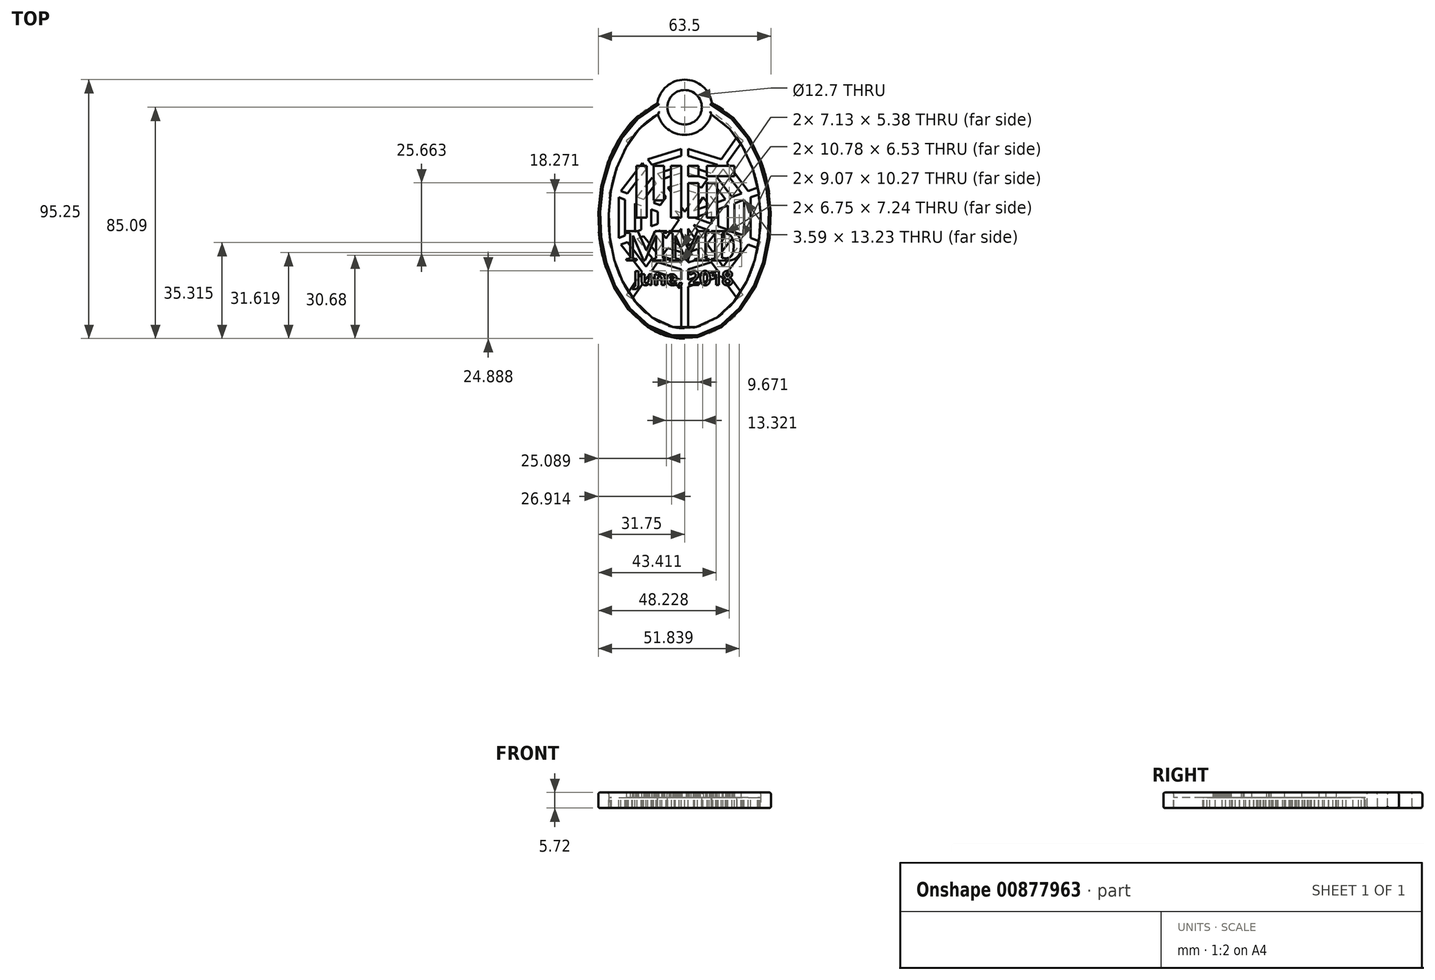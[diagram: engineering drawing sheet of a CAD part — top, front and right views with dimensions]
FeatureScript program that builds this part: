
annotation { "Feature Type Name" : "Feature", "Feature Type Description" : "" }
export const myFeature = defineFeature(function(context is Context, id is Id, definition is map)
    precondition{}
    {
        {
            var Q0;
            Q0=qCreatedBy(makeId("Front.planeOp"),FACE);
            var sketch = newSketch(context, id + "F0", { "sketchPlane" : qUnion([Q0])});
            skLineSegment(sketch, "E0.bottom", {"start": v(31.78, 0) * mm, "end": v(36.86, 0) * mm});
            skLineSegment(sketch, "E0.top", {"start": v(31.78, 5.08) * mm, "end": v(36.86, 5.08) * mm});
            skLineSegment(sketch, "E0.left", {"start": v(31.78, 0) * mm, "end": v(31.78, 5.08) * mm});
            skLineSegment(sketch, "E0.right", {"start": v(36.86, 0) * mm, "end": v(36.86, 5.08) * mm});
            skSolve(sketch);
        }
        {
            var Q0;
            Q0=qCreatedBy(makeId("Top.planeOp"),FACE);
            var sketch = newSketch(context, id + "F1", { "sketchPlane" : qUnion([Q0])});
            skLineSegment(sketch, "E1.bottom", {"start": v(1.27, 40.64) * mm, "end": v(-1.27, 40.64) * mm});
            skLineSegment(sketch, "E1.top", {"start": v(1.27, -40.64) * mm, "end": v(-1.27, -40.64) * mm});
            skLineSegment(sketch, "E1.left", {"start": v(1.27, 40.64) * mm, "end": v(1.27, -40.64) * mm});
            skLineSegment(sketch, "E1.right", {"start": v(-1.27, 40.64) * mm, "end": v(-1.27, -40.64) * mm});
            skPoint(sketch, "E1.middle", {"position": v(0, 0) * mm});
            skLineSegment(sketch, "E2.bottom", {"start": v(21.44, 28.4) * mm, "end": v(19.36, 29.86) * mm});
            skLineSegment(sketch, "E2.top", {"start": v(-19.36, -29.86) * mm, "end": v(-21.44, -28.4) * mm});
            skLineSegment(sketch, "E2.left", {"start": v(21.44, 28.4) * mm, "end": v(-19.36, -29.86) * mm});
            skLineSegment(sketch, "E2.right", {"start": v(19.36, 29.86) * mm, "end": v(-21.44, -28.4) * mm});
            skLineSegment(sketch, "E3.MirrorCS", {"start": v(-19.36, 29.86) * mm, "end": v(-21.44, 28.4) * mm});
            skLineSegment(sketch, "E4.MirrorCS", {"start": v(21.44, -28.4) * mm, "end": v(-19.36, 29.86) * mm});
            skLineSegment(sketch, "E5.MirrorCS", {"start": v(21.44, -28.4) * mm, "end": v(19.36, -29.86) * mm});
            skLineSegment(sketch, "E6.MirrorCS", {"start": v(19.36, -29.86) * mm, "end": v(-21.44, 28.4) * mm});
            skLineSegment(sketch, "E7.bottom", {"start": v(-27.01, -11.18) * mm, "end": v(-27.88, -8.8) * mm});
            skLineSegment(sketch, "E7.top", {"start": v(27.88, 8.8) * mm, "end": v(27.01, 11.18) * mm});
            skLineSegment(sketch, "E7.left", {"start": v(-27.01, -11.18) * mm, "end": v(27.88, 8.8) * mm});
            skLineSegment(sketch, "E7.right", {"start": v(-27.88, -8.8) * mm, "end": v(27.01, 11.18) * mm});
            skEllipse(sketch, "E8", {"center": v(0, 0) * mm, "majorRadius": 44.45 * mm, "minorRadius": 31.75 * mm, "majorAxis": v(0, 1)});
            skLineSegment(sketch, "E9.MirrorCS", {"start": v(-27.01, 11.18) * mm, "end": v(-27.88, 8.8) * mm});
            skLineSegment(sketch, "E10.MirrorCS", {"start": v(-27.88, 8.8) * mm, "end": v(27.01, -11.18) * mm});
            skLineSegment(sketch, "E11.MirrorCS", {"start": v(-27.01, 11.18) * mm, "end": v(27.88, -8.8) * mm});
            skLineSegment(sketch, "E12.MirrorCS", {"start": v(27.88, -8.8) * mm, "end": v(27.01, -11.18) * mm});
            skEllipse(sketch, "E13", {"center": v(0, 0) * mm, "majorRadius": 40.64 * mm, "minorRadius": 27.94 * mm, "majorAxis": v(0, 1)});
            skCircle(sketch, "E14", {"center": v(0, 40.64) * mm, "radius": 6.35 * mm});
            skCircle(sketch, "E15", {"center": v(0, 40.64) * mm, "radius": 10.16 * mm});
            skLineSegment(sketch, "E16", {"start": v(-23.4, 9.87) * mm, "end": v(-15.6, 20.05) * mm});
            skLineSegment(sketch, "E17", {"start": v(-15.6, 20.05) * mm, "end": v(-14.13, 17.97) * mm});
            skLineSegment(sketch, "E18", {"start": v(-14.13, 17.97) * mm, "end": v(-21.01, 9) * mm});
            skLineSegment(sketch, "E19", {"start": v(-21.01, 9) * mm, "end": v(-17.43, 7.7) * mm});
            skLineSegment(sketch, "E20", {"start": v(-17.43, 7.7) * mm, "end": v(-11.94, 14.84) * mm});
            skLineSegment(sketch, "E21", {"start": v(-11.94, 14.84) * mm, "end": v(-10.48, 12.76) * mm});
            skLineSegment(sketch, "E22", {"start": v(-10.48, 12.76) * mm, "end": v(-15.03, 6.82) * mm});
            skLineSegment(sketch, "E23", {"start": v(-15.03, 6.82) * mm, "end": v(-11.44, 5.52) * mm});
            skLineSegment(sketch, "E24", {"start": v(-11.44, 5.52) * mm, "end": v(-8.29, 9.62) * mm});
            skLineSegment(sketch, "E25", {"start": v(-8.29, 9.62) * mm, "end": v(-6.82, 7.53) * mm});
            skLineSegment(sketch, "E26", {"start": v(-6.82, 7.53) * mm, "end": v(-9.04, 4.64) * mm});
            skLineSegment(sketch, "E27", {"start": v(-13.51, 21.5) * mm, "end": v(-1.27, 25.37) * mm});
            skLineSegment(sketch, "E28", {"start": v(-1.27, 25.37) * mm, "end": v(-1.27, 22.82) * mm});
            skLineSegment(sketch, "E29", {"start": v(-1.27, 22.82) * mm, "end": v(-12.05, 19.43) * mm});
            skLineSegment(sketch, "E30", {"start": v(-12.05, 19.43) * mm, "end": v(-9.86, 16.3) * mm});
            skLineSegment(sketch, "E31", {"start": v(-9.86, 16.3) * mm, "end": v(-1.27, 19) * mm});
            skLineSegment(sketch, "E32", {"start": v(-1.27, 19) * mm, "end": v(-1.27, 16.46) * mm});
            skLineSegment(sketch, "E33", {"start": v(-1.27, 16.46) * mm, "end": v(-8.4, 14.21) * mm});
            skLineSegment(sketch, "E34", {"start": v(-6.2, 11.08) * mm, "end": v(-1.27, 12.64) * mm});
            skLineSegment(sketch, "E35", {"start": v(-1.27, 12.64) * mm, "end": v(-1.27, 10.08) * mm});
            skLineSegment(sketch, "E36", {"start": v(-1.27, 10.08) * mm, "end": v(-4.74, 8.99) * mm});
            skLineSegment(sketch, "E37", {"start": v(-24.27, 7.48) * mm, "end": v(-24.27, -7.48) * mm});
            skLineSegment(sketch, "E38", {"start": v(-24.27, -7.48) * mm, "end": v(-21.88, -6.61) * mm});
            skLineSegment(sketch, "E39", {"start": v(-21.88, -6.61) * mm, "end": v(-21.88, 6.61) * mm});
            skLineSegment(sketch, "E40", {"start": v(-21.88, 6.61) * mm, "end": v(-18.3, 5.3) * mm});
            skLineSegment(sketch, "E41", {"start": v(-18.3, 5.3) * mm, "end": v(-18.3, -5.3) * mm});
            skLineSegment(sketch, "E42", {"start": v(-18.3, -5.3) * mm, "end": v(-15.9, -4.44) * mm});
            skLineSegment(sketch, "E43", {"start": v(-15.9, -4.44) * mm, "end": v(-15.9, 4.44) * mm});
            skLineSegment(sketch, "E44", {"start": v(-15.9, 4.44) * mm, "end": v(-12.3, 3.13) * mm});
            skLineSegment(sketch, "E45", {"start": v(-12.3, 3.13) * mm, "end": v(-12.3, -3.13) * mm});
            skLineSegment(sketch, "E46", {"start": v(-12.3, -3.13) * mm, "end": v(-9.9, -2.25) * mm});
            skLineSegment(sketch, "E47", {"start": v(-9.9, -2.25) * mm, "end": v(-9.9, 2.25) * mm});
            skLineSegment(sketch, "E48.MirrorCS", {"start": v(-23.4, -9.87) * mm, "end": v(-15.6, -20.05) * mm});
            skLineSegment(sketch, "E49.MirrorCS", {"start": v(-14.13, -17.97) * mm, "end": v(-21.01, -9) * mm});
            skLineSegment(sketch, "E50.MirrorCS", {"start": v(-17.43, -7.7) * mm, "end": v(-11.94, -14.84) * mm});
            skLineSegment(sketch, "E51.MirrorCS", {"start": v(-10.48, -12.76) * mm, "end": v(-15.03, -6.82) * mm});
            skLineSegment(sketch, "E52.MirrorCS", {"start": v(-11.44, -5.52) * mm, "end": v(-8.29, -9.62) * mm});
            skLineSegment(sketch, "E53.MirrorCS", {"start": v(-6.82, -7.53) * mm, "end": v(-9.04, -4.64) * mm});
            skLineSegment(sketch, "E54.MirrorCS", {"start": v(-1.27, -10.08) * mm, "end": v(-4.74, -8.99) * mm});
            skLineSegment(sketch, "E55.MirrorCS", {"start": v(-6.2, -11.08) * mm, "end": v(-1.27, -12.64) * mm});
            skLineSegment(sketch, "E56.MirrorCS", {"start": v(-1.27, -16.46) * mm, "end": v(-8.4, -14.21) * mm});
            skLineSegment(sketch, "E57.MirrorCS", {"start": v(-9.86, -16.3) * mm, "end": v(-1.27, -19) * mm});
            skLineSegment(sketch, "E58.MirrorCS", {"start": v(-1.27, -22.82) * mm, "end": v(-12.05, -19.43) * mm});
            skLineSegment(sketch, "E59.MirrorCS", {"start": v(-13.51, -21.5) * mm, "end": v(-1.27, -25.37) * mm});
            skPoint(sketch, "E60.endSnap0", {"position": v(0, 44.45) * mm});
            skLineSegment(sketch, "E61.MirrorCS", {"start": v(13.51, 21.5) * mm, "end": v(1.27, 25.37) * mm});
            skLineSegment(sketch, "E62.MirrorCS", {"start": v(1.27, 22.82) * mm, "end": v(12.05, 19.43) * mm});
            skLineSegment(sketch, "E63.MirrorCS", {"start": v(9.86, 16.3) * mm, "end": v(1.27, 19) * mm});
            skLineSegment(sketch, "E64.MirrorCS", {"start": v(1.27, 16.46) * mm, "end": v(8.4, 14.21) * mm});
            skLineSegment(sketch, "E65.MirrorCS", {"start": v(6.2, 11.08) * mm, "end": v(1.27, 12.64) * mm});
            skLineSegment(sketch, "E66.MirrorCS", {"start": v(1.27, 10.08) * mm, "end": v(4.74, 8.99) * mm});
            skLineSegment(sketch, "E67.MirrorCS", {"start": v(6.82, 7.53) * mm, "end": v(9.04, 4.64) * mm});
            skLineSegment(sketch, "E68.MirrorCS", {"start": v(11.44, 5.52) * mm, "end": v(8.29, 9.62) * mm});
            skLineSegment(sketch, "E69.MirrorCS", {"start": v(10.48, 12.76) * mm, "end": v(15.03, 6.82) * mm});
            skLineSegment(sketch, "E70.MirrorCS", {"start": v(17.43, 7.7) * mm, "end": v(11.94, 14.84) * mm});
            skLineSegment(sketch, "E71.MirrorCS", {"start": v(14.13, 17.97) * mm, "end": v(21.01, 9) * mm});
            skLineSegment(sketch, "E72.MirrorCS", {"start": v(23.4, 9.87) * mm, "end": v(15.6, 20.05) * mm});
            skLineSegment(sketch, "E73.MirrorCS", {"start": v(24.27, 7.48) * mm, "end": v(24.27, -7.48) * mm});
            skLineSegment(sketch, "E74.MirrorCS", {"start": v(21.88, -6.61) * mm, "end": v(21.88, 6.61) * mm});
            skLineSegment(sketch, "E75.MirrorCS", {"start": v(18.3, 5.3) * mm, "end": v(18.3, -5.3) * mm});
            skLineSegment(sketch, "E76.MirrorCS", {"start": v(15.9, -4.44) * mm, "end": v(15.9, 4.44) * mm});
            skLineSegment(sketch, "E77.MirrorCS", {"start": v(12.3, 3.13) * mm, "end": v(12.3, -3.13) * mm});
            skLineSegment(sketch, "E78.MirrorCS", {"start": v(9.9, -2.25) * mm, "end": v(9.9, 2.25) * mm});
            skLineSegment(sketch, "E79.MirrorCS", {"start": v(6.82, -7.53) * mm, "end": v(9.04, -4.64) * mm});
            skLineSegment(sketch, "E80.MirrorCS", {"start": v(11.44, -5.52) * mm, "end": v(8.29, -9.62) * mm});
            skLineSegment(sketch, "E81.MirrorCS", {"start": v(10.48, -12.76) * mm, "end": v(15.03, -6.82) * mm});
            skLineSegment(sketch, "E82.MirrorCS", {"start": v(14.13, -17.97) * mm, "end": v(21.01, -9) * mm});
            skLineSegment(sketch, "E83.MirrorCS", {"start": v(23.4, -9.87) * mm, "end": v(15.6, -20.05) * mm});
            skLineSegment(sketch, "E84.MirrorCS", {"start": v(17.43, -7.7) * mm, "end": v(11.94, -14.84) * mm});
            skLineSegment(sketch, "E85.MirrorCS", {"start": v(9.86, -16.3) * mm, "end": v(1.27, -19) * mm});
            skLineSegment(sketch, "E86.MirrorCS", {"start": v(1.27, -22.82) * mm, "end": v(12.05, -19.43) * mm});
            skLineSegment(sketch, "E87.MirrorCS", {"start": v(13.51, -21.5) * mm, "end": v(1.27, -25.37) * mm});
            skLineSegment(sketch, "E88.MirrorCS", {"start": v(1.27, -16.46) * mm, "end": v(8.4, -14.21) * mm});
            skLineSegment(sketch, "E89.MirrorCS", {"start": v(6.2, -11.08) * mm, "end": v(1.27, -12.64) * mm});
            skLineSegment(sketch, "E90.MirrorCS", {"start": v(1.27, -10.08) * mm, "end": v(4.74, -8.99) * mm});
            skSolve(sketch);
        }
        {
            var Q0;
            Q0=qCreatedBy(makeId("Top.planeOp"),FACE);
            var sketch = newSketch(context, id + "F2", { "sketchPlane" : qUnion([Q0])});
            skLineSegment(sketch, "E91.bottom", {"start": v(-13.97, 0) * mm, "end": v(-17.78, 0) * mm});
            skLineSegment(sketch, "E91.top", {"start": v(-13.97, 19.05) * mm, "end": v(-17.78, 19.05) * mm});
            skLineSegment(sketch, "E91.left", {"start": v(-13.97, 0) * mm, "end": v(-13.97, 19.05) * mm});
            skLineSegment(sketch, "E91.right", {"start": v(-17.78, 0) * mm, "end": v(-17.78, 19.05) * mm});
            skLineSegment(sketch, "E92.bottom", {"start": v(-1.27, 0) * mm, "end": v(-5.08, 0) * mm});
            skLineSegment(sketch, "E92.top", {"start": v(-1.27, 19.05) * mm, "end": v(-5.08, 19.05) * mm});
            skLineSegment(sketch, "E92.left", {"start": v(-1.27, 0) * mm, "end": v(-1.27, 19.05) * mm});
            skLineSegment(sketch, "E92.right", {"start": v(-5.08, 0) * mm, "end": v(-5.08, 19.05) * mm});
            skLineSegment(sketch, "E93.bottom", {"start": v(-11.43, 19.05) * mm, "end": v(-7.62, 19.05) * mm});
            skLineSegment(sketch, "E93.top", {"start": v(-11.43, 6.35) * mm, "end": v(-7.62, 6.35) * mm});
            skLineSegment(sketch, "E93.left", {"start": v(-11.43, 19.05) * mm, "end": v(-11.43, 6.35) * mm});
            skLineSegment(sketch, "E93.right", {"start": v(-7.62, 19.05) * mm, "end": v(-7.62, 6.35) * mm});
            skLineSegment(sketch, "E94.bottom", {"start": v(1.3, 19.05) * mm, "end": v(5.1, 19.05) * mm});
            skLineSegment(sketch, "E94.top", {"start": v(1.3, 15.24) * mm, "end": v(5.1, 15.24) * mm});
            skLineSegment(sketch, "E94.left", {"start": v(1.3, 19.05) * mm, "end": v(1.3, 15.24) * mm});
            skLineSegment(sketch, "E94.right", {"start": v(5.1, 19.05) * mm, "end": v(5.1, 15.24) * mm});
            skLineSegment(sketch, "E95.bottom", {"start": v(1.27, 0) * mm, "end": v(5.08, 0) * mm});
            skLineSegment(sketch, "E95.top", {"start": v(1.27, 12.7) * mm, "end": v(5.08, 12.7) * mm});
            skLineSegment(sketch, "E95.left", {"start": v(1.27, 0) * mm, "end": v(1.27, 12.7) * mm});
            skLineSegment(sketch, "E95.right", {"start": v(5.08, 0) * mm, "end": v(5.08, 12.7) * mm});
            skLineSegment(sketch, "E96.bottom", {"start": v(8.1, 19.05) * mm, "end": v(18.26, 19.05) * mm});
            skLineSegment(sketch, "E96.top", {"start": v(8.1, 15.24) * mm, "end": v(18.26, 15.24) * mm});
            skLineSegment(sketch, "E96.left", {"start": v(8.1, 19.05) * mm, "end": v(8.1, 15.24) * mm});
            skLineSegment(sketch, "E96.right", {"start": v(18.26, 19.05) * mm, "end": v(18.26, 15.24) * mm});
            skLineSegment(sketch, "E97.bottom", {"start": v(8.1, 12.7) * mm, "end": v(11.91, 12.7) * mm});
            skLineSegment(sketch, "E97.top", {"start": v(8.1, 0) * mm, "end": v(11.91, 0) * mm});
            skLineSegment(sketch, "E97.left", {"start": v(8.1, 12.7) * mm, "end": v(8.1, 0) * mm});
            skLineSegment(sketch, "E97.right", {"start": v(11.91, 12.7) * mm, "end": v(11.91, 0) * mm});
            skText(sketch, "E98", { "text": "MMD", "fontName": "Tinos-Bold.ttf"});
            skText(sketch, "E99", { "text": "June, 2018", "fontName": "OpenSans-Bold.ttf"});
            const initialGuessF2  = {"E98": [-0.02175, -0.01575, 1, 0, 0.01194], "E99": [-0.01872, -0.02477, 1, 0, 0.0052]};
            skSetInitialGuess(sketch, initialGuessF2);
            skSolve(sketch);
        }
        {
            var Q0;
            {var subQ0=sQuery(id+"F1.wireOp",EDGE,"E15");var subQ1=sQuery(id+"F1.wireOp",EDGE,"E8");var subQ2=makeQuery(id+"F1.imprint","INTERSECT",VERTEX,{"disambiguationData":[OD(0.0)],"derivedFrom":[subQ1,subQ0]});Q0=makeQuery(id+"F1.imprint","IMPRINT",FACE,{"disambiguationData":[TD([[makeQuery(id+"F1.imprint","IMPRINT",EDGE,{"disambiguationData":[TD([[subQ2,1.0]])],"derivedFrom":subQ1}),-1.0]])]});}
            var Q1;
            {var subQ0=sQuery(id+"F1.wireOp",EDGE,"E15");var subQ1=sQuery(id+"F1.wireOp",EDGE,"E8");var subQ2=makeQuery(id+"F1.imprint","INTERSECT",VERTEX,{"disambiguationData":[OD(0.0)],"derivedFrom":[subQ1,subQ0]});Q1=makeQuery(id+"F1.imprint","IMPRINT",FACE,{"disambiguationData":[TD([[makeQuery(id+"F1.imprint","IMPRINT",EDGE,{"disambiguationData":[TD([[subQ2,1.0]])],"derivedFrom":subQ1}),1.0]])]});}
            var Q2;
            {var subQ0=sQuery(id+"F1.wireOp",EDGE,"E14");var subQ1=sQuery(id+"F1.wireOp",EDGE,"E1.right");var subQ2=makeQuery(id+"F1.imprint","INTERSECT",VERTEX,{"derivedFrom":[subQ1,subQ0]});Q2=makeQuery(id+"F1.imprint","IMPRINT",FACE,{"disambiguationData":[TD([[makeQuery(id+"F1.imprint","IMPRINT",EDGE,{"disambiguationData":[TD([[subQ2,-1.0]])],"derivedFrom":subQ1}),-1.0]])]});}
            var Q3;
            {var subQ0=sQuery(id+"F1.wireOp",EDGE,"E14");var subQ1=sQuery(id+"F1.wireOp",EDGE,"E1.left");var subQ2=makeQuery(id+"F1.imprint","INTERSECT",VERTEX,{"derivedFrom":[subQ1,subQ0]});Q3=makeQuery(id+"F1.imprint","IMPRINT",FACE,{"disambiguationData":[TD([[makeQuery(id+"F1.imprint","IMPRINT",EDGE,{"disambiguationData":[TD([[subQ2,-1.0]])],"derivedFrom":subQ1}),-1.0]])]});}
            var Q4;
            {var subQ0=sQuery(id+"F1.wireOp",EDGE,"E14");var subQ1=sQuery(id+"F1.wireOp",EDGE,"E1.left");var subQ2=makeQuery(id+"F1.imprint","INTERSECT",VERTEX,{"derivedFrom":[subQ1,subQ0]});Q4=makeQuery(id+"F1.imprint","IMPRINT",FACE,{"disambiguationData":[TD([[makeQuery(id+"F1.imprint","IMPRINT",EDGE,{"disambiguationData":[TD([[subQ2,-1.0]])],"derivedFrom":subQ1}),1.0]])]});}
            var Q5;
            {var subQ0=sQuery(id+"F1.wireOp",EDGE,"E15");var subQ1=sQuery(id+"F1.wireOp",EDGE,"E8");var subQ2=makeQuery(id+"F1.imprint","INTERSECT",VERTEX,{"disambiguationData":[OD(1.0)],"derivedFrom":[subQ1,subQ0]});Q5=makeQuery(id+"F1.imprint","IMPRINT",FACE,{"disambiguationData":[TD([[makeQuery(id+"F1.imprint","IMPRINT",EDGE,{"disambiguationData":[TD([[subQ2,-1.0]])],"derivedFrom":subQ1}),1.0]])]});}
            var Q6;
            {var subQ34=sQuery(id+"F1.wireOp",EDGE,"E2.bottom");Q6=makeQuery(id+"F1.imprint","IMPRINT",FACE,{"disambiguationData":[TD([[makeQuery(id+"F1.imprint","IMPRINT",EDGE,{"derivedFrom":subQ34}),-1.0]])]});}
            extrude(context, id + "F3", {"entities" : qUnion([Q0, Q1, Q2, Q3, Q4, Q5, Q6]), "depth" : -3.8 * mm, "offsetDistance" : 25.4 * mm});
        }
        {
            var Q0;
            {var subQ0=sQuery(id+"F1.wireOp",EDGE,"E15");var subQ1=sQuery(id+"F1.wireOp",EDGE,"E8");var subQ2=makeQuery(id+"F1.imprint","INTERSECT",VERTEX,{"disambiguationData":[OD(0.0)],"derivedFrom":[subQ1,subQ0]});Q0=makeQuery(id+"F1.imprint","IMPRINT",FACE,{"disambiguationData":[TD([[makeQuery(id+"F1.imprint","IMPRINT",EDGE,{"disambiguationData":[TD([[subQ2,1.0]])],"derivedFrom":subQ1}),-1.0]])]});}
            var Q1;
            {var subQ0=sQuery(id+"F1.wireOp",EDGE,"E15");var subQ1=sQuery(id+"F1.wireOp",EDGE,"E8");var subQ2=makeQuery(id+"F1.imprint","INTERSECT",VERTEX,{"disambiguationData":[OD(0.0)],"derivedFrom":[subQ1,subQ0]});Q1=makeQuery(id+"F1.imprint","IMPRINT",FACE,{"disambiguationData":[TD([[makeQuery(id+"F1.imprint","IMPRINT",EDGE,{"disambiguationData":[TD([[subQ2,1.0]])],"derivedFrom":subQ1}),1.0]])]});}
            var Q2;
            {var subQ0=sQuery(id+"F1.wireOp",EDGE,"E14");var subQ1=sQuery(id+"F1.wireOp",EDGE,"E1.right");var subQ2=makeQuery(id+"F1.imprint","INTERSECT",VERTEX,{"derivedFrom":[subQ1,subQ0]});Q2=makeQuery(id+"F1.imprint","IMPRINT",FACE,{"disambiguationData":[TD([[makeQuery(id+"F1.imprint","IMPRINT",EDGE,{"disambiguationData":[TD([[subQ2,-1.0]])],"derivedFrom":subQ1}),-1.0]])]});}
            var Q3;
            {var subQ0=sQuery(id+"F1.wireOp",EDGE,"E14");var subQ1=sQuery(id+"F1.wireOp",EDGE,"E1.left");var subQ2=makeQuery(id+"F1.imprint","INTERSECT",VERTEX,{"derivedFrom":[subQ1,subQ0]});Q3=makeQuery(id+"F1.imprint","IMPRINT",FACE,{"disambiguationData":[TD([[makeQuery(id+"F1.imprint","IMPRINT",EDGE,{"disambiguationData":[TD([[subQ2,-1.0]])],"derivedFrom":subQ1}),-1.0]])]});}
            var Q4;
            {var subQ0=sQuery(id+"F1.wireOp",EDGE,"E14");var subQ1=sQuery(id+"F1.wireOp",EDGE,"E1.left");var subQ2=makeQuery(id+"F1.imprint","INTERSECT",VERTEX,{"derivedFrom":[subQ1,subQ0]});Q4=makeQuery(id+"F1.imprint","IMPRINT",FACE,{"disambiguationData":[TD([[makeQuery(id+"F1.imprint","IMPRINT",EDGE,{"disambiguationData":[TD([[subQ2,-1.0]])],"derivedFrom":subQ1}),1.0]])]});}
            var Q5;
            {var subQ0=sQuery(id+"F1.wireOp",EDGE,"E15");var subQ1=sQuery(id+"F1.wireOp",EDGE,"E8");var subQ2=makeQuery(id+"F1.imprint","INTERSECT",VERTEX,{"disambiguationData":[OD(1.0)],"derivedFrom":[subQ1,subQ0]});Q5=makeQuery(id+"F1.imprint","IMPRINT",FACE,{"disambiguationData":[TD([[makeQuery(id+"F1.imprint","IMPRINT",EDGE,{"disambiguationData":[TD([[subQ2,-1.0]])],"derivedFrom":subQ1}),1.0]])]});}
            var Q6;
            {var subQ34=sQuery(id+"F1.wireOp",EDGE,"E2.bottom");Q6=makeQuery(id+"F1.imprint","IMPRINT",FACE,{"disambiguationData":[TD([[makeQuery(id+"F1.imprint","IMPRINT",EDGE,{"derivedFrom":subQ34}),-1.0]])]});}
            var Q7;
            {var subQ0=sQuery(id+"F1.wireOp",EDGE,"E2.bottom");Q7=makeQuery(id+"F1.imprint","IMPRINT",FACE,{"disambiguationData":[TD([[makeQuery(id+"F1.imprint","IMPRINT",EDGE,{"derivedFrom":subQ0}),1.0]])]});}
            var Q8;
            {var subQ0=sQuery(id+"F1.wireOp",EDGE,"E7.top");Q8=makeQuery(id+"F1.imprint","IMPRINT",FACE,{"disambiguationData":[TD([[makeQuery(id+"F1.imprint","IMPRINT",EDGE,{"derivedFrom":subQ0}),1.0]])]});}
            var Q9;
            {var subQ0=sQuery(id+"F1.wireOp",EDGE,"E3.MirrorCS");Q9=makeQuery(id+"F1.imprint","IMPRINT",FACE,{"disambiguationData":[TD([[makeQuery(id+"F1.imprint","IMPRINT",EDGE,{"derivedFrom":subQ0}),1.0]])]});}
            var Q10;
            {var subQ0=sQuery(id+"F1.wireOp",EDGE,"E9.MirrorCS");Q10=makeQuery(id+"F1.imprint","IMPRINT",FACE,{"disambiguationData":[TD([[makeQuery(id+"F1.imprint","IMPRINT",EDGE,{"derivedFrom":subQ0}),1.0]])]});}
            var Q11;
            {var subQ0=sQuery(id+"F1.wireOp",EDGE,"E7.bottom");Q11=makeQuery(id+"F1.imprint","IMPRINT",FACE,{"disambiguationData":[TD([[makeQuery(id+"F1.imprint","IMPRINT",EDGE,{"derivedFrom":subQ0}),-1.0]])]});}
            var Q12;
            {var subQ0=sQuery(id+"F1.wireOp",EDGE,"E12.MirrorCS");Q12=makeQuery(id+"F1.imprint","IMPRINT",FACE,{"disambiguationData":[TD([[makeQuery(id+"F1.imprint","IMPRINT",EDGE,{"derivedFrom":subQ0}),-1.0]])]});}
            var Q13;
            {var subQ0=sQuery(id+"F1.wireOp",EDGE,"E5.MirrorCS");Q13=makeQuery(id+"F1.imprint","IMPRINT",FACE,{"disambiguationData":[TD([[makeQuery(id+"F1.imprint","IMPRINT",EDGE,{"derivedFrom":subQ0}),-1.0]])]});}
            var Q14;
            {var subQ0=sQuery(id+"F1.wireOp",EDGE,"E1.right");var subQ1=sQuery(id+"F1.wireOp",EDGE,"E1.top");var subQ2=makeQuery(id+"F1.imprint","INTERSECT",VERTEX,{"derivedFrom":[subQ1,subQ0]});Q14=makeQuery(id+"F1.imprint","IMPRINT",FACE,{"disambiguationData":[TD([[makeQuery(id+"F1.imprint","IMPRINT",EDGE,{"disambiguationData":[TD([[subQ2,1.0]])],"derivedFrom":subQ1}),-1.0]])]});}
            var Q15;
            {var subQ0=sQuery(id+"F1.wireOp",EDGE,"E1.left");var subQ1=sQuery(id+"F1.wireOp",EDGE,"E1.top");var subQ2=makeQuery(id+"F1.imprint","INTERSECT",VERTEX,{"derivedFrom":[subQ1,subQ0]});Q15=makeQuery(id+"F1.imprint","IMPRINT",FACE,{"disambiguationData":[TD([[makeQuery(id+"F1.imprint","IMPRINT",EDGE,{"disambiguationData":[TD([[subQ2,-1.0]])],"derivedFrom":subQ1}),-1.0]])]});}
            var Q16;
            {var subQ0=sQuery(id+"F1.wireOp",EDGE,"E2.top");Q16=makeQuery(id+"F1.imprint","IMPRINT",FACE,{"disambiguationData":[TD([[makeQuery(id+"F1.imprint","IMPRINT",EDGE,{"derivedFrom":subQ0}),-1.0]])]});}
            extrude(context, id + "F4", {"entities" : qUnion([Q0, Q1, Q2, Q3, Q4, Q5, Q6, Q7, Q8, Q9, Q10, Q11, Q12, Q13, Q14, Q15, Q16]), "operationType" : NewBodyOperationType.ADD, "depth" : 1.9 * mm, "offsetDistance" : 25.4 * mm});
        }
        {
            var Q0;
            {var subQ0=sQuery(id+"F1.wireOp",EDGE,"E7.top");Q0=makeQuery(id+"F1.imprint","IMPRINT",FACE,{"disambiguationData":[TD([[makeQuery(id+"F1.imprint","IMPRINT",EDGE,{"derivedFrom":subQ0}),1.0]])]});}
            var Q1;
            {var subQ0=sQuery(id+"F1.wireOp",EDGE,"E9.MirrorCS");Q1=makeQuery(id+"F1.imprint","IMPRINT",FACE,{"disambiguationData":[TD([[makeQuery(id+"F1.imprint","IMPRINT",EDGE,{"derivedFrom":subQ0}),1.0]])]});}
            var Q2;
            {var subQ15=sQuery(id+"F1.wireOp",EDGE,"E19");Q2=makeQuery(id+"F1.imprint","IMPRINT",FACE,{"disambiguationData":[TD([[makeQuery(id+"F1.imprint","IMPRINT",EDGE,{"derivedFrom":subQ15}),-1.0]])]});}
            var Q3;
            {var subQ0=sQuery(id+"F1.wireOp",EDGE,"E7.right");var subQ1=sQuery(id+"F1.wireOp",EDGE,"E1.right");var subQ2=makeQuery(id+"F1.imprint","INTERSECT",VERTEX,{"derivedFrom":[subQ1,subQ0]});Q3=makeQuery(id+"F1.imprint","IMPRINT",FACE,{"disambiguationData":[TD([[makeQuery(id+"F1.imprint","IMPRINT",EDGE,{"disambiguationData":[TD([[subQ2,-1.0]])],"derivedFrom":subQ1}),-1.0]])]});}
            var Q4;
            {var subQ5=sQuery(id+"F1.wireOp",EDGE,"E17");Q4=makeQuery(id+"F1.imprint","IMPRINT",FACE,{"disambiguationData":[TD([[makeQuery(id+"F1.imprint","IMPRINT",EDGE,{"derivedFrom":subQ5}),1.0]])]});}
            var Q5;
            {var subQ0=sQuery(id+"F1.wireOp",EDGE,"E11.MirrorCS");var subQ1=sQuery(id+"F1.wireOp",EDGE,"E1.right");var subQ2=makeQuery(id+"F1.imprint","INTERSECT",VERTEX,{"derivedFrom":[subQ1,subQ0]});Q5=makeQuery(id+"F1.imprint","IMPRINT",FACE,{"disambiguationData":[TD([[makeQuery(id+"F1.imprint","IMPRINT",EDGE,{"disambiguationData":[TD([[subQ2,-1.0]])],"derivedFrom":subQ1}),-1.0]])]});}
            var Q6;
            {var subQ0=sQuery(id+"F1.wireOp",EDGE,"E6.MirrorCS");var subQ1=sQuery(id+"F1.wireOp",EDGE,"E2.right");var subQ2=makeQuery(id+"F1.imprint","INTERSECT",VERTEX,{"derivedFrom":[subQ1,subQ0]});Q6=makeQuery(id+"F1.imprint","IMPRINT",FACE,{"disambiguationData":[TD([[makeQuery(id+"F1.imprint","IMPRINT",EDGE,{"disambiguationData":[TD([[subQ2,-1.0]])],"derivedFrom":subQ1}),-1.0]])]});}
            var Q7;
            {var subQ0=sQuery(id+"F1.wireOp",EDGE,"E7.right");var subQ1=sQuery(id+"F1.wireOp",EDGE,"E1.right");var subQ2=makeQuery(id+"F1.imprint","INTERSECT",VERTEX,{"derivedFrom":[subQ1,subQ0]});Q7=makeQuery(id+"F1.imprint","IMPRINT",FACE,{"disambiguationData":[TD([[makeQuery(id+"F1.imprint","IMPRINT",EDGE,{"disambiguationData":[TD([[subQ2,-1.0]])],"derivedFrom":subQ1}),1.0]])]});}
            var Q8;
            {var subQ0=sQuery(id+"F1.wireOp",EDGE,"E2.right");var subQ1=sQuery(id+"F1.wireOp",EDGE,"E1.right");var subQ2=makeQuery(id+"F1.imprint","INTERSECT",VERTEX,{"derivedFrom":[subQ1,subQ0]});Q8=makeQuery(id+"F1.imprint","IMPRINT",FACE,{"disambiguationData":[TD([[makeQuery(id+"F1.imprint","IMPRINT",EDGE,{"disambiguationData":[TD([[subQ2,-1.0]])],"derivedFrom":subQ1}),-1.0]])]});}
            var Q9;
            {var subQ4=sQuery(id+"F1.wireOp",EDGE,"E2.right");var subQ5=sQuery(id+"F1.wireOp",EDGE,"E1.left");var subQ6=makeQuery(id+"F1.imprint","INTERSECT",VERTEX,{"derivedFrom":[subQ5,subQ4]});Q9=makeQuery(id+"F1.imprint","IMPRINT",FACE,{"disambiguationData":[TD([[makeQuery(id+"F1.imprint","IMPRINT",EDGE,{"disambiguationData":[TD([[subQ6,-1.0]])],"derivedFrom":subQ5}),1.0]])]});}
            var Q10;
            {var subQ0=sQuery(id+"F1.wireOp",EDGE,"E2.top");Q10=makeQuery(id+"F1.imprint","IMPRINT",FACE,{"disambiguationData":[TD([[makeQuery(id+"F1.imprint","IMPRINT",EDGE,{"derivedFrom":subQ0}),-1.0]])]});}
            var Q11;
            {var subQ2=sQuery(id+"F1.wireOp",EDGE,"E10.MirrorCS");var subQ6=sQuery(id+"F1.wireOp",EDGE,"E1.left");var subQ14=makeQuery(id+"F1.imprint","INTERSECT",VERTEX,{"derivedFrom":[subQ6,subQ2]});Q11=makeQuery(id+"F1.imprint","IMPRINT",FACE,{"disambiguationData":[TD([[makeQuery(id+"F1.imprint","IMPRINT",EDGE,{"disambiguationData":[TD([[subQ14,-1.0]])],"derivedFrom":subQ6}),1.0]])]});}
            var Q12;
            {var subQ0=sQuery(id+"F1.wireOp",EDGE,"E10.MirrorCS");var subQ1=sQuery(id+"F1.wireOp",EDGE,"E2.left");var subQ2=makeQuery(id+"F1.imprint","INTERSECT",VERTEX,{"derivedFrom":[subQ1,subQ0]});Q12=makeQuery(id+"F1.imprint","IMPRINT",FACE,{"disambiguationData":[TD([[makeQuery(id+"F1.imprint","IMPRINT",EDGE,{"disambiguationData":[TD([[subQ2,-1.0]])],"derivedFrom":subQ1}),-1.0]])]});}
            var Q13;
            {var subQ0=sQuery(id+"F1.wireOp",EDGE,"E1.left");var subQ1=sQuery(id+"F1.wireOp",EDGE,"E1.top");var subQ2=makeQuery(id+"F1.imprint","INTERSECT",VERTEX,{"derivedFrom":[subQ1,subQ0]});Q13=makeQuery(id+"F1.imprint","IMPRINT",FACE,{"disambiguationData":[TD([[makeQuery(id+"F1.imprint","IMPRINT",EDGE,{"disambiguationData":[TD([[subQ2,-1.0]])],"derivedFrom":subQ1}),-1.0]])]});}
            var Q14;
            {var subQ0=sQuery(id+"F1.wireOp",EDGE,"E2.right");var subQ1=sQuery(id+"F1.wireOp",EDGE,"E1.left");var subQ2=makeQuery(id+"F1.imprint","INTERSECT",VERTEX,{"derivedFrom":[subQ1,subQ0]});Q14=makeQuery(id+"F1.imprint","IMPRINT",FACE,{"disambiguationData":[TD([[makeQuery(id+"F1.imprint","IMPRINT",EDGE,{"disambiguationData":[TD([[subQ2,-1.0]])],"derivedFrom":subQ1}),-1.0]])]});}
            var Q15;
            {var subQ0=sQuery(id+"F1.wireOp",EDGE,"E10.MirrorCS");var subQ1=sQuery(id+"F1.wireOp",EDGE,"E1.right");var subQ2=makeQuery(id+"F1.imprint","INTERSECT",VERTEX,{"derivedFrom":[subQ1,subQ0]});Q15=makeQuery(id+"F1.imprint","IMPRINT",FACE,{"disambiguationData":[TD([[makeQuery(id+"F1.imprint","IMPRINT",EDGE,{"disambiguationData":[TD([[subQ2,-1.0]])],"derivedFrom":subQ1}),-1.0]])]});}
            var Q16;
            {var subQ0=sQuery(id+"F1.wireOp",EDGE,"E2.left");var subQ1=sQuery(id+"F1.wireOp",EDGE,"E1.left");var subQ2=makeQuery(id+"F1.imprint","INTERSECT",VERTEX,{"derivedFrom":[subQ1,subQ0]});Q16=makeQuery(id+"F1.imprint","IMPRINT",FACE,{"disambiguationData":[TD([[makeQuery(id+"F1.imprint","IMPRINT",EDGE,{"disambiguationData":[TD([[subQ2,-1.0]])],"derivedFrom":subQ1}),1.0]])]});}
            var Q17;
            {var subQ0=sQuery(id+"F1.wireOp",EDGE,"E10.MirrorCS");var subQ1=sQuery(id+"F1.wireOp",EDGE,"E1.left");var subQ2=makeQuery(id+"F1.imprint","INTERSECT",VERTEX,{"derivedFrom":[subQ1,subQ0]});Q17=makeQuery(id+"F1.imprint","IMPRINT",FACE,{"disambiguationData":[TD([[makeQuery(id+"F1.imprint","IMPRINT",EDGE,{"disambiguationData":[TD([[subQ2,-1.0]])],"derivedFrom":subQ1}),-1.0]])]});}
            var Q18;
            {var subQ0=sQuery(id+"F1.wireOp",EDGE,"E11.MirrorCS");var subQ1=sQuery(id+"F1.wireOp",EDGE,"E2.left");var subQ2=makeQuery(id+"F1.imprint","INTERSECT",VERTEX,{"derivedFrom":[subQ1,subQ0]});Q18=makeQuery(id+"F1.imprint","IMPRINT",FACE,{"disambiguationData":[TD([[makeQuery(id+"F1.imprint","IMPRINT",EDGE,{"disambiguationData":[TD([[subQ2,-1.0]])],"derivedFrom":subQ1}),1.0]])]});}
            var Q19;
            {var subQ0=sQuery(id+"F1.wireOp",EDGE,"E7.right");var subQ3=sQuery(id+"F1.wireOp",EDGE,"E2.left");var subQ4=makeQuery(id+"F1.imprint","INTERSECT",VERTEX,{"derivedFrom":[subQ3,subQ0]});Q19=makeQuery(id+"F1.imprint","IMPRINT",FACE,{"disambiguationData":[TD([[makeQuery(id+"F1.imprint","IMPRINT",EDGE,{"disambiguationData":[TD([[subQ4,-1.0]])],"derivedFrom":subQ3}),1.0]])]});}
            var Q20;
            {var subQ16=sQuery(id+"F1.wireOp",EDGE,"E38");Q20=makeQuery(id+"F1.imprint","IMPRINT",FACE,{"disambiguationData":[TD([[makeQuery(id+"F1.imprint","IMPRINT",EDGE,{"derivedFrom":subQ16}),-1.0]])]});}
            var Q21;
            {var subQ4=sQuery(id+"F1.wireOp",EDGE,"E10.MirrorCS");var subQ16=sQuery(id+"F1.wireOp",EDGE,"E4.MirrorCS");var subQ20=makeQuery(id+"F1.imprint","INTERSECT",VERTEX,{"derivedFrom":[subQ16,subQ4]});Q21=makeQuery(id+"F1.imprint","IMPRINT",FACE,{"disambiguationData":[TD([[makeQuery(id+"F1.imprint","IMPRINT",EDGE,{"disambiguationData":[TD([[subQ20,-1.0]])],"derivedFrom":subQ16}),-1.0]])]});}
            var Q22;
            {var subQ0=sQuery(id+"F1.wireOp",EDGE,"E1.left");var subQ13=makeQuery(id+"F1.imprint","INTERSECT",VERTEX,{"derivedFrom":[subQ0,sQuery(id+"F1.wireOp",EDGE,"E90.MirrorCS")]});Q22=makeQuery(id+"F1.imprint","IMPRINT",FACE,{"disambiguationData":[TD([[makeQuery(id+"F1.imprint","IMPRINT",EDGE,{"disambiguationData":[TD([[subQ13,1.0]])],"derivedFrom":subQ0}),-1.0]])]});}
            var Q23;
            {var subQ0=sQuery(id+"F1.wireOp",EDGE,"E4.MirrorCS");var subQ1=sQuery(id+"F1.wireOp",EDGE,"E2.right");var subQ2=makeQuery(id+"F1.imprint","INTERSECT",VERTEX,{"derivedFrom":[subQ1,subQ0]});Q23=makeQuery(id+"F1.imprint","IMPRINT",FACE,{"disambiguationData":[TD([[makeQuery(id+"F1.imprint","IMPRINT",EDGE,{"disambiguationData":[TD([[subQ2,-1.0]])],"derivedFrom":subQ1}),1.0]])]});}
            var Q24;
            {var subQ0=sQuery(id+"F1.wireOp",EDGE,"E12.MirrorCS");Q24=makeQuery(id+"F1.imprint","IMPRINT",FACE,{"disambiguationData":[TD([[makeQuery(id+"F1.imprint","IMPRINT",EDGE,{"derivedFrom":subQ0}),-1.0]])]});}
            var Q25;
            {var subQ0=sQuery(id+"F1.wireOp",EDGE,"E7.right");var subQ1=sQuery(id+"F1.wireOp",EDGE,"E1.left");var subQ2=makeQuery(id+"F1.imprint","INTERSECT",VERTEX,{"derivedFrom":[subQ1,subQ0]});Q25=makeQuery(id+"F1.imprint","IMPRINT",FACE,{"disambiguationData":[TD([[makeQuery(id+"F1.imprint","IMPRINT",EDGE,{"disambiguationData":[TD([[subQ2,-1.0]])],"derivedFrom":subQ1}),1.0]])]});}
            var Q26;
            {var subQ0=sQuery(id+"F1.wireOp",EDGE,"E7.left");var subQ1=sQuery(id+"F1.wireOp",EDGE,"E1.right");var subQ2=makeQuery(id+"F1.imprint","INTERSECT",VERTEX,{"derivedFrom":[subQ1,subQ0]});Q26=makeQuery(id+"F1.imprint","IMPRINT",FACE,{"disambiguationData":[TD([[makeQuery(id+"F1.imprint","IMPRINT",EDGE,{"disambiguationData":[TD([[subQ2,-1.0]])],"derivedFrom":subQ1}),1.0]])]});}
            var Q27;
            {var subQ13=sQuery(id+"F1.wireOp",EDGE,"E7.left");var subQ14=sQuery(id+"F1.wireOp",EDGE,"E1.right");var subQ15=makeQuery(id+"F1.imprint","INTERSECT",VERTEX,{"derivedFrom":[subQ14,subQ13]});Q27=makeQuery(id+"F1.imprint","IMPRINT",FACE,{"disambiguationData":[TD([[makeQuery(id+"F1.imprint","IMPRINT",EDGE,{"disambiguationData":[TD([[subQ15,-1.0]])],"derivedFrom":subQ14}),-1.0]])]});}
            var Q28;
            {var subQ0=sQuery(id+"F1.wireOp",EDGE,"E6.MirrorCS");var subQ1=sQuery(id+"F1.wireOp",EDGE,"E1.right");var subQ2=makeQuery(id+"F1.imprint","INTERSECT",VERTEX,{"derivedFrom":[subQ1,subQ0]});Q28=makeQuery(id+"F1.imprint","IMPRINT",FACE,{"disambiguationData":[TD([[makeQuery(id+"F1.imprint","IMPRINT",EDGE,{"disambiguationData":[TD([[subQ2,-1.0]])],"derivedFrom":subQ1}),-1.0]])]});}
            var Q29;
            {var subQ0=sQuery(id+"F1.wireOp",EDGE,"E7.left");var subQ1=sQuery(id+"F1.wireOp",EDGE,"E1.left");var subQ2=makeQuery(id+"F1.imprint","INTERSECT",VERTEX,{"derivedFrom":[subQ1,subQ0]});Q29=makeQuery(id+"F1.imprint","IMPRINT",FACE,{"disambiguationData":[TD([[makeQuery(id+"F1.imprint","IMPRINT",EDGE,{"disambiguationData":[TD([[subQ2,-1.0]])],"derivedFrom":subQ1}),1.0]])]});}
            var Q30;
            {var subQ0=sQuery(id+"F1.wireOp",EDGE,"E4.MirrorCS");var subQ1=sQuery(id+"F1.wireOp",EDGE,"E1.right");var subQ2=makeQuery(id+"F1.imprint","INTERSECT",VERTEX,{"derivedFrom":[subQ1,subQ0]});Q30=makeQuery(id+"F1.imprint","IMPRINT",FACE,{"disambiguationData":[TD([[makeQuery(id+"F1.imprint","IMPRINT",EDGE,{"disambiguationData":[TD([[subQ2,-1.0]])],"derivedFrom":subQ1}),1.0]])]});}
            var Q31;
            {var subQ0=sQuery(id+"F1.wireOp",EDGE,"E4.MirrorCS");var subQ1=sQuery(id+"F1.wireOp",EDGE,"E1.left");var subQ2=makeQuery(id+"F1.imprint","INTERSECT",VERTEX,{"derivedFrom":[subQ1,subQ0]});Q31=makeQuery(id+"F1.imprint","IMPRINT",FACE,{"disambiguationData":[TD([[makeQuery(id+"F1.imprint","IMPRINT",EDGE,{"disambiguationData":[TD([[subQ2,-1.0]])],"derivedFrom":subQ1}),1.0]])]});}
            var Q32;
            {var subQ0=sQuery(id+"F1.wireOp",EDGE,"E7.left");var subQ1=sQuery(id+"F1.wireOp",EDGE,"E1.left");var subQ2=makeQuery(id+"F1.imprint","INTERSECT",VERTEX,{"derivedFrom":[subQ1,subQ0]});Q32=makeQuery(id+"F1.imprint","IMPRINT",FACE,{"disambiguationData":[TD([[makeQuery(id+"F1.imprint","IMPRINT",EDGE,{"disambiguationData":[TD([[subQ2,-1.0]])],"derivedFrom":subQ1}),-1.0]])]});}
            var Q33;
            {var subQ0=sQuery(id+"F1.wireOp",EDGE,"E7.left");var subQ1=sQuery(id+"F1.wireOp",EDGE,"E6.MirrorCS");var subQ2=makeQuery(id+"F1.imprint","INTERSECT",VERTEX,{"derivedFrom":[subQ1,subQ0]});Q33=makeQuery(id+"F1.imprint","IMPRINT",FACE,{"disambiguationData":[TD([[makeQuery(id+"F1.imprint","IMPRINT",EDGE,{"disambiguationData":[TD([[subQ2,-1.0]])],"derivedFrom":subQ1}),-1.0]])]});}
            var Q34;
            {var subQ0=sQuery(id+"F1.wireOp",EDGE,"E11.MirrorCS");var subQ1=sQuery(id+"F1.wireOp",EDGE,"E1.left");var subQ2=makeQuery(id+"F1.imprint","INTERSECT",VERTEX,{"derivedFrom":[subQ1,subQ0]});Q34=makeQuery(id+"F1.imprint","IMPRINT",FACE,{"disambiguationData":[TD([[makeQuery(id+"F1.imprint","IMPRINT",EDGE,{"disambiguationData":[TD([[subQ2,-1.0]])],"derivedFrom":subQ1}),1.0]])]});}
            var Q35;
            {var subQ0=sQuery(id+"F1.wireOp",EDGE,"E11.MirrorCS");var subQ1=sQuery(id+"F1.wireOp",EDGE,"E1.left");var subQ2=makeQuery(id+"F1.imprint","INTERSECT",VERTEX,{"derivedFrom":[subQ1,subQ0]});Q35=makeQuery(id+"F1.imprint","IMPRINT",FACE,{"disambiguationData":[TD([[makeQuery(id+"F1.imprint","IMPRINT",EDGE,{"disambiguationData":[TD([[subQ2,-1.0]])],"derivedFrom":subQ1}),-1.0]])]});}
            var Q36;
            {var subQ0=sQuery(id+"F1.wireOp",EDGE,"E10.MirrorCS");var subQ1=sQuery(id+"F1.wireOp",EDGE,"E1.right");var subQ2=makeQuery(id+"F1.imprint","INTERSECT",VERTEX,{"derivedFrom":[subQ1,subQ0]});Q36=makeQuery(id+"F1.imprint","IMPRINT",FACE,{"disambiguationData":[TD([[makeQuery(id+"F1.imprint","IMPRINT",EDGE,{"disambiguationData":[TD([[subQ2,-1.0]])],"derivedFrom":subQ1}),1.0]])]});}
            var Q37;
            {var subQ0=sQuery(id+"F1.wireOp",EDGE,"E2.left");var subQ1=sQuery(id+"F1.wireOp",EDGE,"E1.left");var subQ2=makeQuery(id+"F1.imprint","INTERSECT",VERTEX,{"derivedFrom":[subQ1,subQ0]});Q37=makeQuery(id+"F1.imprint","IMPRINT",FACE,{"disambiguationData":[TD([[makeQuery(id+"F1.imprint","IMPRINT",EDGE,{"disambiguationData":[TD([[subQ2,-1.0]])],"derivedFrom":subQ1}),-1.0]])]});}
            var Q38;
            {var subQ0=sQuery(id+"F1.wireOp",EDGE,"E7.left");var subQ1=sQuery(id+"F1.wireOp",EDGE,"E2.left");var subQ2=makeQuery(id+"F1.imprint","INTERSECT",VERTEX,{"derivedFrom":[subQ1,subQ0]});Q38=makeQuery(id+"F1.imprint","IMPRINT",FACE,{"disambiguationData":[TD([[makeQuery(id+"F1.imprint","IMPRINT",EDGE,{"disambiguationData":[TD([[subQ2,-1.0]])],"derivedFrom":subQ1}),-1.0]])]});}
            var Q39;
            {var subQ0=sQuery(id+"F1.wireOp",EDGE,"E7.right");var subQ1=sQuery(id+"F1.wireOp",EDGE,"E1.left");var subQ2=makeQuery(id+"F1.imprint","INTERSECT",VERTEX,{"derivedFrom":[subQ1,subQ0]});Q39=makeQuery(id+"F1.imprint","IMPRINT",FACE,{"disambiguationData":[TD([[makeQuery(id+"F1.imprint","IMPRINT",EDGE,{"disambiguationData":[TD([[subQ2,-1.0]])],"derivedFrom":subQ1}),-1.0]])]});}
            var Q40;
            {var subQ0=sQuery(id+"F1.wireOp",EDGE,"E11.MirrorCS");var subQ1=sQuery(id+"F1.wireOp",EDGE,"E1.right");var subQ2=makeQuery(id+"F1.imprint","INTERSECT",VERTEX,{"derivedFrom":[subQ1,subQ0]});Q40=makeQuery(id+"F1.imprint","IMPRINT",FACE,{"disambiguationData":[TD([[makeQuery(id+"F1.imprint","IMPRINT",EDGE,{"disambiguationData":[TD([[subQ2,-1.0]])],"derivedFrom":subQ1}),1.0]])]});}
            var Q41;
            {var subQ0=sQuery(id+"F1.wireOp",EDGE,"E6.MirrorCS");var subQ1=sQuery(id+"F1.wireOp",EDGE,"E1.right");var subQ2=makeQuery(id+"F1.imprint","INTERSECT",VERTEX,{"derivedFrom":[subQ1,subQ0]});Q41=makeQuery(id+"F1.imprint","IMPRINT",FACE,{"disambiguationData":[TD([[makeQuery(id+"F1.imprint","IMPRINT",EDGE,{"disambiguationData":[TD([[subQ2,-1.0]])],"derivedFrom":subQ1}),1.0]])]});}
            var Q42;
            {var subQ0=sQuery(id+"F1.wireOp",EDGE,"E11.MirrorCS");var subQ1=sQuery(id+"F1.wireOp",EDGE,"E4.MirrorCS");var subQ2=makeQuery(id+"F1.imprint","INTERSECT",VERTEX,{"derivedFrom":[subQ1,subQ0]});Q42=makeQuery(id+"F1.imprint","IMPRINT",FACE,{"disambiguationData":[TD([[makeQuery(id+"F1.imprint","IMPRINT",EDGE,{"disambiguationData":[TD([[subQ2,-1.0]])],"derivedFrom":subQ1}),1.0]])]});}
            var Q43;
            {var subQ1=sQuery(id+"F1.wireOp",EDGE,"E1.left");var subQ10=sQuery(id+"F1.wireOp",EDGE,"E4.MirrorCS");var subQ11=makeQuery(id+"F1.imprint","INTERSECT",VERTEX,{"derivedFrom":[subQ1,subQ10]});Q43=makeQuery(id+"F1.imprint","IMPRINT",FACE,{"disambiguationData":[TD([[makeQuery(id+"F1.imprint","IMPRINT",EDGE,{"disambiguationData":[TD([[subQ11,-1.0]])],"derivedFrom":subQ1}),-1.0]])]});}
            var Q44;
            {var subQ0=sQuery(id+"F1.wireOp",EDGE,"E11.MirrorCS");var subQ1=sQuery(id+"F1.wireOp",EDGE,"E2.right");var subQ2=makeQuery(id+"F1.imprint","INTERSECT",VERTEX,{"derivedFrom":[subQ1,subQ0]});Q44=makeQuery(id+"F1.imprint","IMPRINT",FACE,{"disambiguationData":[TD([[makeQuery(id+"F1.imprint","IMPRINT",EDGE,{"disambiguationData":[TD([[subQ2,-1.0]])],"derivedFrom":subQ1}),1.0]])]});}
            var Q45;
            {var subQ0=sQuery(id+"F1.wireOp",EDGE,"E7.bottom");Q45=makeQuery(id+"F1.imprint","IMPRINT",FACE,{"disambiguationData":[TD([[makeQuery(id+"F1.imprint","IMPRINT",EDGE,{"derivedFrom":subQ0}),-1.0]])]});}
            var Q46;
            {var subQ0=sQuery(id+"F1.wireOp",EDGE,"E5.MirrorCS");Q46=makeQuery(id+"F1.imprint","IMPRINT",FACE,{"disambiguationData":[TD([[makeQuery(id+"F1.imprint","IMPRINT",EDGE,{"derivedFrom":subQ0}),-1.0]])]});}
            var Q47;
            {var subQ0=sQuery(id+"F1.wireOp",EDGE,"E1.right");var subQ1=sQuery(id+"F1.wireOp",EDGE,"E1.top");var subQ2=makeQuery(id+"F1.imprint","INTERSECT",VERTEX,{"derivedFrom":[subQ1,subQ0]});Q47=makeQuery(id+"F1.imprint","IMPRINT",FACE,{"disambiguationData":[TD([[makeQuery(id+"F1.imprint","IMPRINT",EDGE,{"disambiguationData":[TD([[subQ2,1.0]])],"derivedFrom":subQ1}),-1.0]])]});}
            var Q48;
            {var subQ0=sQuery(id+"F1.wireOp",EDGE,"E3.MirrorCS");Q48=makeQuery(id+"F1.imprint","IMPRINT",FACE,{"disambiguationData":[TD([[makeQuery(id+"F1.imprint","IMPRINT",EDGE,{"derivedFrom":subQ0}),1.0]])]});}
            var Q49;
            {var subQ0=sQuery(id+"F1.wireOp",EDGE,"E2.bottom");Q49=makeQuery(id+"F1.imprint","IMPRINT",FACE,{"disambiguationData":[TD([[makeQuery(id+"F1.imprint","IMPRINT",EDGE,{"derivedFrom":subQ0}),1.0]])]});}
            var Q50;
            {var subQ11=sQuery(id+"F1.wireOp",EDGE,"E28");Q50=makeQuery(id+"F1.imprint","IMPRINT",FACE,{"disambiguationData":[TD([[makeQuery(id+"F1.imprint","IMPRINT",EDGE,{"derivedFrom":subQ11}),1.0]])]});}
            var Q51;
            {var subQ0=sQuery(id+"F1.wireOp",EDGE,"E61.MirrorCS");Q51=makeQuery(id+"F1.imprint","IMPRINT",FACE,{"disambiguationData":[TD([[makeQuery(id+"F1.imprint","IMPRINT",EDGE,{"derivedFrom":subQ0}),1.0]])]});}
            var Q52;
            {var subQ0=sQuery(id+"F1.wireOp",EDGE,"E27");Q52=makeQuery(id+"F1.imprint","IMPRINT",FACE,{"disambiguationData":[TD([[makeQuery(id+"F1.imprint","IMPRINT",EDGE,{"derivedFrom":subQ0}),-1.0]])]});}
            var Q53;
            {var subQ0=sQuery(id+"F1.wireOp",EDGE,"E31");Q53=makeQuery(id+"F1.imprint","IMPRINT",FACE,{"disambiguationData":[TD([[makeQuery(id+"F1.imprint","IMPRINT",EDGE,{"derivedFrom":subQ0}),-1.0]])]});}
            var Q54;
            {var subQ0=sQuery(id+"F1.wireOp",EDGE,"E34");Q54=makeQuery(id+"F1.imprint","IMPRINT",FACE,{"disambiguationData":[TD([[makeQuery(id+"F1.imprint","IMPRINT",EDGE,{"derivedFrom":subQ0}),-1.0]])]});}
            var Q55;
            {var subQ0=sQuery(id+"F1.wireOp",EDGE,"E65.MirrorCS");Q55=makeQuery(id+"F1.imprint","IMPRINT",FACE,{"disambiguationData":[TD([[makeQuery(id+"F1.imprint","IMPRINT",EDGE,{"derivedFrom":subQ0}),1.0]])]});}
            var Q56;
            {var subQ0=sQuery(id+"F1.wireOp",EDGE,"E63.MirrorCS");Q56=makeQuery(id+"F1.imprint","IMPRINT",FACE,{"disambiguationData":[TD([[makeQuery(id+"F1.imprint","IMPRINT",EDGE,{"derivedFrom":subQ0}),1.0]])]});}
            var Q57;
            {var subQ0=sQuery(id+"F1.wireOp",EDGE,"E71.MirrorCS");Q57=makeQuery(id+"F1.imprint","IMPRINT",FACE,{"disambiguationData":[TD([[makeQuery(id+"F1.imprint","IMPRINT",EDGE,{"derivedFrom":subQ0}),1.0]])]});}
            var Q58;
            {var subQ0=sQuery(id+"F1.wireOp",EDGE,"E69.MirrorCS");Q58=makeQuery(id+"F1.imprint","IMPRINT",FACE,{"disambiguationData":[TD([[makeQuery(id+"F1.imprint","IMPRINT",EDGE,{"derivedFrom":subQ0}),1.0]])]});}
            var Q59;
            {var subQ0=sQuery(id+"F1.wireOp",EDGE,"E67.MirrorCS");Q59=makeQuery(id+"F1.imprint","IMPRINT",FACE,{"disambiguationData":[TD([[makeQuery(id+"F1.imprint","IMPRINT",EDGE,{"derivedFrom":subQ0}),1.0]])]});}
            var Q60;
            {var subQ0=sQuery(id+"F1.wireOp",EDGE,"E77.MirrorCS");Q60=makeQuery(id+"F1.imprint","IMPRINT",FACE,{"disambiguationData":[TD([[makeQuery(id+"F1.imprint","IMPRINT",EDGE,{"derivedFrom":subQ0}),-1.0]])]});}
            var Q61;
            {var subQ0=sQuery(id+"F1.wireOp",EDGE,"E75.MirrorCS");Q61=makeQuery(id+"F1.imprint","IMPRINT",FACE,{"disambiguationData":[TD([[makeQuery(id+"F1.imprint","IMPRINT",EDGE,{"derivedFrom":subQ0}),-1.0]])]});}
            var Q62;
            {var subQ0=sQuery(id+"F1.wireOp",EDGE,"E73.MirrorCS");Q62=makeQuery(id+"F1.imprint","IMPRINT",FACE,{"disambiguationData":[TD([[makeQuery(id+"F1.imprint","IMPRINT",EDGE,{"derivedFrom":subQ0}),-1.0]])]});}
            var Q63;
            {var subQ0=sQuery(id+"F1.wireOp",EDGE,"E82.MirrorCS");Q63=makeQuery(id+"F1.imprint","IMPRINT",FACE,{"disambiguationData":[TD([[makeQuery(id+"F1.imprint","IMPRINT",EDGE,{"derivedFrom":subQ0}),-1.0]])]});}
            var Q64;
            {var subQ0=sQuery(id+"F1.wireOp",EDGE,"E81.MirrorCS");Q64=makeQuery(id+"F1.imprint","IMPRINT",FACE,{"disambiguationData":[TD([[makeQuery(id+"F1.imprint","IMPRINT",EDGE,{"derivedFrom":subQ0}),-1.0]])]});}
            var Q65;
            {var subQ0=sQuery(id+"F1.wireOp",EDGE,"E79.MirrorCS");Q65=makeQuery(id+"F1.imprint","IMPRINT",FACE,{"disambiguationData":[TD([[makeQuery(id+"F1.imprint","IMPRINT",EDGE,{"derivedFrom":subQ0}),-1.0]])]});}
            var Q66;
            {var subQ0=sQuery(id+"F1.wireOp",EDGE,"E89.MirrorCS");Q66=makeQuery(id+"F1.imprint","IMPRINT",FACE,{"disambiguationData":[TD([[makeQuery(id+"F1.imprint","IMPRINT",EDGE,{"derivedFrom":subQ0}),-1.0]])]});}
            var Q67;
            {var subQ0=sQuery(id+"F1.wireOp",EDGE,"E85.MirrorCS");Q67=makeQuery(id+"F1.imprint","IMPRINT",FACE,{"disambiguationData":[TD([[makeQuery(id+"F1.imprint","IMPRINT",EDGE,{"derivedFrom":subQ0}),-1.0]])]});}
            var Q68;
            {var subQ0=sQuery(id+"F1.wireOp",EDGE,"E86.MirrorCS");Q68=makeQuery(id+"F1.imprint","IMPRINT",FACE,{"disambiguationData":[TD([[makeQuery(id+"F1.imprint","IMPRINT",EDGE,{"derivedFrom":subQ0}),-1.0]])]});}
            var Q69;
            {var subQ0=sQuery(id+"F1.wireOp",EDGE,"E58.MirrorCS");Q69=makeQuery(id+"F1.imprint","IMPRINT",FACE,{"disambiguationData":[TD([[makeQuery(id+"F1.imprint","IMPRINT",EDGE,{"derivedFrom":subQ0}),1.0]])]});}
            var Q70;
            {var subQ0=sQuery(id+"F1.wireOp",EDGE,"E56.MirrorCS");Q70=makeQuery(id+"F1.imprint","IMPRINT",FACE,{"disambiguationData":[TD([[makeQuery(id+"F1.imprint","IMPRINT",EDGE,{"derivedFrom":subQ0}),1.0]])]});}
            var Q71;
            {var subQ0=sQuery(id+"F1.wireOp",EDGE,"E54.MirrorCS");Q71=makeQuery(id+"F1.imprint","IMPRINT",FACE,{"disambiguationData":[TD([[makeQuery(id+"F1.imprint","IMPRINT",EDGE,{"derivedFrom":subQ0}),1.0]])]});}
            var Q72;
            {var subQ0=sQuery(id+"F1.wireOp",EDGE,"E52.MirrorCS");Q72=makeQuery(id+"F1.imprint","IMPRINT",FACE,{"disambiguationData":[TD([[makeQuery(id+"F1.imprint","IMPRINT",EDGE,{"derivedFrom":subQ0}),1.0]])]});}
            var Q73;
            {var subQ0=sQuery(id+"F1.wireOp",EDGE,"E50.MirrorCS");Q73=makeQuery(id+"F1.imprint","IMPRINT",FACE,{"disambiguationData":[TD([[makeQuery(id+"F1.imprint","IMPRINT",EDGE,{"derivedFrom":subQ0}),1.0]])]});}
            var Q74;
            {var subQ0=sQuery(id+"F1.wireOp",EDGE,"E48.MirrorCS");Q74=makeQuery(id+"F1.imprint","IMPRINT",FACE,{"disambiguationData":[TD([[makeQuery(id+"F1.imprint","IMPRINT",EDGE,{"derivedFrom":subQ0}),1.0]])]});}
            var Q75;
            {var subQ0=sQuery(id+"F1.wireOp",EDGE,"E37");Q75=makeQuery(id+"F1.imprint","IMPRINT",FACE,{"disambiguationData":[TD([[makeQuery(id+"F1.imprint","IMPRINT",EDGE,{"derivedFrom":subQ0}),1.0]])]});}
            var Q76;
            {var subQ0=sQuery(id+"F1.wireOp",EDGE,"E41");Q76=makeQuery(id+"F1.imprint","IMPRINT",FACE,{"disambiguationData":[TD([[makeQuery(id+"F1.imprint","IMPRINT",EDGE,{"derivedFrom":subQ0}),1.0]])]});}
            var Q77;
            {var subQ0=sQuery(id+"F1.wireOp",EDGE,"E45");Q77=makeQuery(id+"F1.imprint","IMPRINT",FACE,{"disambiguationData":[TD([[makeQuery(id+"F1.imprint","IMPRINT",EDGE,{"derivedFrom":subQ0}),1.0]])]});}
            var Q78;
            {var subQ0=sQuery(id+"F1.wireOp",EDGE,"E24");Q78=makeQuery(id+"F1.imprint","IMPRINT",FACE,{"disambiguationData":[TD([[makeQuery(id+"F1.imprint","IMPRINT",EDGE,{"derivedFrom":subQ0}),-1.0]])]});}
            var Q79;
            {var subQ0=sQuery(id+"F1.wireOp",EDGE,"E20");Q79=makeQuery(id+"F1.imprint","IMPRINT",FACE,{"disambiguationData":[TD([[makeQuery(id+"F1.imprint","IMPRINT",EDGE,{"derivedFrom":subQ0}),-1.0]])]});}
            var Q80;
            {var subQ0=sQuery(id+"F1.wireOp",EDGE,"E16");Q80=makeQuery(id+"F1.imprint","IMPRINT",FACE,{"disambiguationData":[TD([[makeQuery(id+"F1.imprint","IMPRINT",EDGE,{"derivedFrom":subQ0}),-1.0]])]});}
            extrude(context, id + "F5", {"entities" : qUnion([Q0, Q1, Q2, Q3, Q4, Q5, Q6, Q7, Q8, Q9, Q10, Q11, Q12, Q13, Q14, Q15, Q16, Q17, Q18, Q19, Q20, Q21, Q22, Q23, Q24, Q25, Q26, Q27, Q28, Q29, Q30, Q31, Q32, Q33, Q34, Q35, Q36, Q37, Q38, Q39, Q40, Q41, Q42, Q43, Q44, Q45, Q46, Q47, Q48, Q49, Q50, Q51, Q52, Q53, Q54, Q55, Q56, Q57, Q58, Q59, Q60, Q61, Q62, Q63, Q64, Q65, Q66, Q67, Q68, Q69, Q70, Q71, Q72, Q73, Q74, Q75, Q76, Q77, Q78, Q79, Q80]), "depth" : -3.8 * mm, "offsetDistance" : 25.4 * mm});
        }
        {
            var Q0;
            Q0=makeQuery(id+"F2.imprint","IMPRINT",FACE,{"disambiguationData":[TD([[makeQuery(id+"F2.imprint","IMPRINT",EDGE,{"derivedFrom":sQuery(id+"F2.wireOp",EDGE,"E92.bottom")}),-1.0]])]});
            var Q1;
            Q1=makeQuery(id+"F2.imprint","IMPRINT",FACE,{"disambiguationData":[TD([[makeQuery(id+"F2.imprint","IMPRINT",EDGE,{"derivedFrom":sQuery(id+"F2.wireOp",EDGE,"E93.bottom")}),-1.0]])]});
            var Q2;
            Q2=makeQuery(id+"F2.imprint","IMPRINT",FACE,{"disambiguationData":[TD([[makeQuery(id+"F2.imprint","IMPRINT",EDGE,{"derivedFrom":sQuery(id+"F2.wireOp",EDGE,"E91.bottom")}),-1.0]])]});
            var Q3;
            Q3=makeQuery(id+"F2.imprint","IMPRINT",FACE,{"disambiguationData":[TD([[makeQuery(id+"F2.imprint","IMPRINT",EDGE,{"derivedFrom":sQuery(id+"F2.wireOp",EDGE,"E94.bottom")}),-1.0]])]});
            var Q4;
            Q4=makeQuery(id+"F2.imprint","IMPRINT",FACE,{"disambiguationData":[TD([[makeQuery(id+"F2.imprint","IMPRINT",EDGE,{"derivedFrom":sQuery(id+"F2.wireOp",EDGE,"E95.bottom")}),1.0]])]});
            var Q5;
            Q5=makeQuery(id+"F2.imprint","IMPRINT",FACE,{"disambiguationData":[TD([[makeQuery(id+"F2.imprint","IMPRINT",EDGE,{"derivedFrom":sQuery(id+"F2.wireOp",EDGE,"E96.bottom")}),-1.0]])]});
            var Q6;
            Q6=makeQuery(id+"F2.imprint","IMPRINT",FACE,{"disambiguationData":[TD([[makeQuery(id+"F2.imprint","IMPRINT",EDGE,{"derivedFrom":sQuery(id+"F2.wireOp",EDGE,"E97.bottom")}),-1.0]])]});
            extrude(context, id + "F6", {"entities" : qUnion([Q0, Q1, Q2, Q3, Q4, Q5, Q6]), "depth" : 1.9 * mm, "offsetDistance" : 25.4 * mm});
        }
        {
            var Q0;
            Q0=qSketchRegion(id+"F2",true);
            extrude(context, id + "F7", {"entities" : qUnion([Q0]), "depth" : 1.9 * mm, "offsetDistance" : 25.4 * mm});
        }
        {
            var Q0;
            Q0=makeQuery(id+"F4.opExtrude","CAP_EDGE",EDGE,{"disambiguationData":[OSD([sQuery(id+"F1.wireOp",EDGE,"E14")])],"isStart":false});
            var Q1;
            Q1=makeQuery(id+"F4.opExtrude","CAP_EDGE",EDGE,{"disambiguationData":[OSD([sQuery(id+"F1.wireOp",EDGE,"E8")])],"isStart":false});
            var Q2;
            Q2=makeQuery(id+"F4.opExtrude","CAP_EDGE",EDGE,{"disambiguationData":[OSD([sQuery(id+"F1.wireOp",EDGE,"E13")])],"isStart":false});
            var Q3;
            {var subQ0=sQuery(id+"F1.wireOp",EDGE,"E15");var subQ1=makeQuery(id+"F1.imprint","INTERSECT",VERTEX,{"derivedFrom":[sQuery(id+"F1.wireOp",EDGE,"E1.left"),subQ0]});var subQ3=makeQuery(id+"F1.imprint","INTERSECT",VERTEX,{"derivedFrom":[sQuery(id+"F1.wireOp",EDGE,"E1.right"),subQ0]});Q3=makeQuery(id+"F4.opExtrude","CAP_EDGE",EDGE,{"disambiguationData":[OSD([subQ0]),TDD([makeQuery(id+"F1.imprint","IMPRINT",EDGE,{"disambiguationData":[TD([[subQ3,1.0]])],"derivedFrom":subQ0}),makeQuery(id+"F1.imprint","IMPRINT",EDGE,{"disambiguationData":[TD([[subQ1,1.0]])],"derivedFrom":subQ0}),makeQuery(id+"F1.imprint","IMPRINT",EDGE,{"disambiguationData":[TD([[subQ1,-1.0]])],"derivedFrom":subQ0})])],"isStart":false});}
            var Q4;
            {var subQ0=sQuery(id+"F1.wireOp",EDGE,"E15");var subQ1=sQuery(id+"F1.wireOp",EDGE,"E8");Q4=makeQuery(id+"F4.opExtrude","CAP_EDGE",EDGE,{"disambiguationData":[OSD([subQ0]),TDD([makeQuery(id+"F1.imprint","IMPRINT",EDGE,{"disambiguationData":[TD([[makeQuery(id+"F1.imprint","INTERSECT",VERTEX,{"disambiguationData":[OD(0.0)],"derivedFrom":[subQ1,subQ0]}),1.0]])],"derivedFrom":subQ0})])],"isStart":false});}
            var Q5;
            {var subQ3=sQuery(id+"F1.wireOp",EDGE,"E15");var subQ4=sQuery(id+"F1.wireOp",EDGE,"E1.left");var subQ5=makeQuery(id+"F1.imprint","INTERSECT",VERTEX,{"derivedFrom":[subQ4,subQ3]});var subQ7=makeQuery(id+"F1.imprint","IMPRINT",EDGE,{"disambiguationData":[TD([[subQ5,-1.0]])],"derivedFrom":subQ3});var subQ8=sQuery(id+"F1.wireOp",EDGE,"E1.right");var subQ9=makeQuery(id+"F1.imprint","INTERSECT",VERTEX,{"derivedFrom":[subQ8,subQ3]});var subQ10=makeQuery(id+"F1.imprint","IMPRINT",EDGE,{"disambiguationData":[TD([[subQ5,1.0]])],"derivedFrom":subQ3});var subQ12=makeQuery(id+"F1.imprint","IMPRINT",EDGE,{"disambiguationData":[TD([[subQ9,1.0]])],"derivedFrom":subQ3});Q5=makeQuery(id+"F5.boolean.opBoolean","SPLIT",EDGE,{"disambiguationData":[TD([makeQuery(id+"F5.opExtrude","SWEPT_FACE",FACE,{"disambiguationData":[OSD([subQ4]),TDD([makeQuery(id+"F1.imprint","IMPRINT",EDGE,{"disambiguationData":[TD([[subQ5,-1.0]])],"derivedFrom":subQ4})])]})])],"derivedFrom":makeQuery(id+"F3.opExtrude","CAP_EDGE",EDGE,{"disambiguationData":[OSD([subQ3]),TDD([subQ12,subQ10,subQ7])],"isStart":false})});}
            var Q6;
            {var subQ0=sQuery(id+"F1.wireOp",EDGE,"E13");Q6=makeQuery(id+"F3.opExtrude","CAP_EDGE",EDGE,{"disambiguationData":[OSD([subQ0]),TDD([makeQuery(id+"F1.imprint","IMPRINT",EDGE,{"disambiguationData":[TD([[makeQuery(id+"F1.imprint","INTERSECT",VERTEX,{"disambiguationData":[OD(0.0)],"derivedFrom":[sQuery(id+"F1.wireOp",EDGE,"E2.right"),subQ0]}),-1.0]])],"derivedFrom":subQ0})])],"isStart":false});}
            var Q7;
            {var subQ0=sQuery(id+"F1.wireOp",EDGE,"E13");Q7=makeQuery(id+"F3.opExtrude","CAP_EDGE",EDGE,{"disambiguationData":[OSD([subQ0]),TDD([makeQuery(id+"F1.imprint","IMPRINT",EDGE,{"disambiguationData":[TD([[makeQuery(id+"F1.imprint","INTERSECT",VERTEX,{"disambiguationData":[OD(1.0)],"derivedFrom":[sQuery(id+"F1.wireOp",EDGE,"E4.MirrorCS"),subQ0]}),1.0]])],"derivedFrom":subQ0})])],"isStart":false});}
            var Q8;
            Q8=makeQuery(id+"F3.opExtrude","CAP_EDGE",EDGE,{"disambiguationData":[OSD([sQuery(id+"F1.wireOp",EDGE,"E8")])],"isStart":false});
            var Q9;
            {var subQ3=sQuery(id+"F1.wireOp",EDGE,"E15");var subQ4=sQuery(id+"F1.wireOp",EDGE,"E1.left");var subQ5=makeQuery(id+"F1.imprint","INTERSECT",VERTEX,{"derivedFrom":[subQ4,subQ3]});var subQ7=makeQuery(id+"F1.imprint","IMPRINT",EDGE,{"disambiguationData":[TD([[subQ5,-1.0]])],"derivedFrom":subQ3});var subQ8=sQuery(id+"F1.wireOp",EDGE,"E1.right");var subQ9=makeQuery(id+"F1.imprint","INTERSECT",VERTEX,{"derivedFrom":[subQ8,subQ3]});var subQ10=makeQuery(id+"F1.imprint","IMPRINT",EDGE,{"disambiguationData":[TD([[subQ5,1.0]])],"derivedFrom":subQ3});var subQ12=makeQuery(id+"F1.imprint","IMPRINT",EDGE,{"disambiguationData":[TD([[subQ9,1.0]])],"derivedFrom":subQ3});Q9=makeQuery(id+"F5.boolean.opBoolean","SPLIT",EDGE,{"disambiguationData":[TD([makeQuery(id+"F5.opExtrude","SWEPT_FACE",FACE,{"disambiguationData":[OSD([subQ8]),TDD([makeQuery(id+"F1.imprint","IMPRINT",EDGE,{"disambiguationData":[TD([[subQ9,-1.0]])],"derivedFrom":subQ8})])]})])],"derivedFrom":makeQuery(id+"F3.opExtrude","CAP_EDGE",EDGE,{"disambiguationData":[OSD([subQ3]),TDD([subQ12,subQ10,subQ7])],"isStart":false})});}
            var Q10;
            {var subQ0=sQuery(id+"F1.wireOp",EDGE,"E15");var subQ1=sQuery(id+"F1.wireOp",EDGE,"E8");Q10=makeQuery(id+"F3.opExtrude","CAP_EDGE",EDGE,{"disambiguationData":[OSD([subQ0]),TDD([makeQuery(id+"F1.imprint","IMPRINT",EDGE,{"disambiguationData":[TD([[makeQuery(id+"F1.imprint","INTERSECT",VERTEX,{"disambiguationData":[OD(0.0)],"derivedFrom":[subQ1,subQ0]}),1.0]])],"derivedFrom":subQ0})])],"isStart":false});}
            var Q11;
            Q11=makeQuery(id+"F3.opExtrude","CAP_EDGE",EDGE,{"disambiguationData":[OSD([sQuery(id+"F1.wireOp",EDGE,"E14")])],"isStart":false});
            fillet(context, id + "F8", {"entities" : qUnion([Q0, Q1, Q2, Q3, Q4, Q5, Q6, Q7, Q8, Q9, Q10, Q11]), "radius" : 0.64 * mm, "tangentPropagation" : true, "allowEdgeOverflow" : false});
        }
        {
            var Q0;
            Q0=makeQuery(id+"F7.opExtrude","SWEPT_BODY",BODY,{"disambiguationData":[OSD([sQuery(id+"F2.wireOp",EDGE,"E91.bottom"),sQuery(id+"F2.wireOp",EDGE,"E91.top"),sQuery(id+"F2.wireOp",EDGE,"E91.left"),sQuery(id+"F2.wireOp",EDGE,"E91.right")])]});
            var Q1;
            Q1=makeQuery(id+"F7.opExtrude","SWEPT_BODY",BODY,{"disambiguationData":[OSD([sQuery(id+"F2.wireOp",EDGE,"E92.bottom"),sQuery(id+"F2.wireOp",EDGE,"E92.top"),sQuery(id+"F2.wireOp",EDGE,"E92.left"),sQuery(id+"F2.wireOp",EDGE,"E92.right")])]});
            var Q2;
            Q2=makeQuery(id+"F7.opExtrude","SWEPT_BODY",BODY,{"disambiguationData":[OSD([sQuery(id+"F2.wireOp",EDGE,"E93.bottom"),sQuery(id+"F2.wireOp",EDGE,"E93.top"),sQuery(id+"F2.wireOp",EDGE,"E93.left"),sQuery(id+"F2.wireOp",EDGE,"E93.right")])]});
            var Q3;
            Q3=makeQuery(id+"F7.opExtrude","SWEPT_BODY",BODY,{"disambiguationData":[OSD([sQuery(id+"F2.wireOp",EDGE,"E94.bottom"),sQuery(id+"F2.wireOp",EDGE,"E94.top"),sQuery(id+"F2.wireOp",EDGE,"E94.left"),sQuery(id+"F2.wireOp",EDGE,"E94.right")])]});
            var Q4;
            Q4=makeQuery(id+"F7.opExtrude","SWEPT_BODY",BODY,{"disambiguationData":[OSD([sQuery(id+"F2.wireOp",EDGE,"E95.bottom"),sQuery(id+"F2.wireOp",EDGE,"E95.top"),sQuery(id+"F2.wireOp",EDGE,"E95.left"),sQuery(id+"F2.wireOp",EDGE,"E95.right")])]});
            var Q5;
            Q5=makeQuery(id+"F7.opExtrude","SWEPT_BODY",BODY,{"disambiguationData":[OSD([sQuery(id+"F2.wireOp",EDGE,"E96.bottom"),sQuery(id+"F2.wireOp",EDGE,"E96.top"),sQuery(id+"F2.wireOp",EDGE,"E96.left"),sQuery(id+"F2.wireOp",EDGE,"E96.right")])]});
            var Q6;
            Q6=makeQuery(id+"F7.opExtrude","SWEPT_BODY",BODY,{"disambiguationData":[OSD([sQuery(id+"F2.wireOp",EDGE,"E97.bottom"),sQuery(id+"F2.wireOp",EDGE,"E97.top"),sQuery(id+"F2.wireOp",EDGE,"E97.left"),sQuery(id+"F2.wireOp",EDGE,"E97.right")])]});
            deleteBodies(context, id + "F9", {"entities" : qUnion([Q0, Q1, Q2, Q3, Q4, Q5, Q6])});
        }
    });
